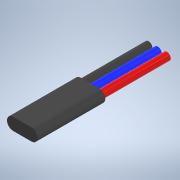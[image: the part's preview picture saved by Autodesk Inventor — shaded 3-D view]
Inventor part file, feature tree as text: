
AUTODESK INVENTOR PART (.ipt)
format: ipt  version: 2022 (Build 260153000, 153)  size: 120,320 bytes
history: native  units: in
note: dims shown in document units (in); Inventor stores cm internally (conversion verified against a paired STEP export)
features: extrude x2, sketch x2
ambient origin geometry x8: Origin, YZ Plane, XZ Plane, XY Plane, X Axis, Y Axis, Z Axis, Center Point
bodies: Solid1 (feature_tree)
feature tree (4):
  extrude  "Extrusion1"  Depth=0.1575in
  extrude  "Extrusion2"  Depth=0.875in
  sketch  "Sketch1"  dims[d0=0.1575in d1=0.2362in]
  sketch  "Sketch2"  dims[d2=0.875in d3=0.0in d4=0.0984in d5=0.0984in d6=0.7874in d8=360.0deg d10=0.875in d11=0.0in]
